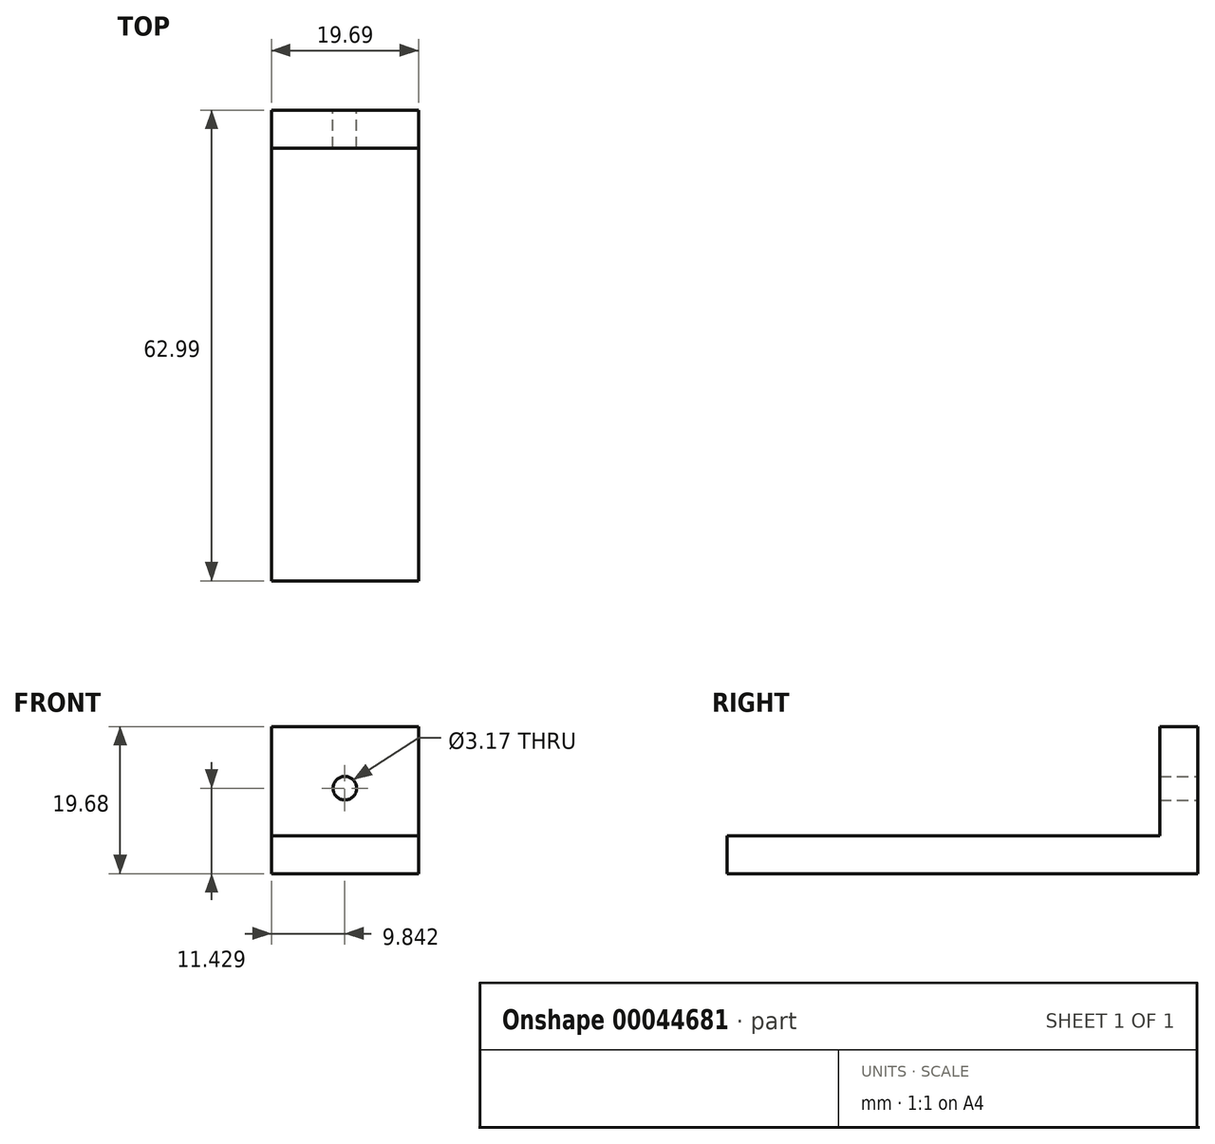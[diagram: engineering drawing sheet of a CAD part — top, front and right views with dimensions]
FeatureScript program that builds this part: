
annotation { "Feature Type Name" : "Feature", "Feature Type Description" : "" }
export const myFeature = defineFeature(function(context is Context, id is Id, definition is map)
    precondition{}
    {
        {
            var Q0;
            Q0=qCreatedBy(makeId("Right.planeOp"),FACE);
            var sketch = newSketch(context, id + "F0", { "sketchPlane" : qUnion([Q0])});
            skLineSegment(sketch, "E0", {"start": v(-35.25, -15.6) * mm, "end": v(27.74, -15.6) * mm});
            skLineSegment(sketch, "E1", {"start": v(27.74, -15.6) * mm, "end": v(27.74, 4.08) * mm});
            skLineSegment(sketch, "E2", {"start": v(27.74, 4.08) * mm, "end": v(22.66, 4.08) * mm});
            skLineSegment(sketch, "E3", {"start": v(22.66, 4.08) * mm, "end": v(22.66, -10.52) * mm});
            skLineSegment(sketch, "E4", {"start": v(22.66, -10.52) * mm, "end": v(-35.25, -10.52) * mm});
            skLineSegment(sketch, "E5", {"start": v(-35.25, -10.52) * mm, "end": v(-35.25, -15.6) * mm});
            skSolve(sketch);
        }
        {
            var Q0;
            Q0=makeQuery(id+"F0.imprint","IMPRINT",FACE,{"disambiguationData":[TD([[makeQuery(id+"F0.imprint","IMPRINT",EDGE,{"derivedFrom":sQuery(id+"F0.wireOp",EDGE,"E0")}),1.0]])]});
            extrude(context, id + "F1", {"entities" : qUnion([Q0]), "depth" : 19.68 * mm});
        }
        {
            var Q0;
            Q0=makeQuery(id+"F1.opExtrude","SWEPT_FACE",FACE,{"disambiguationData":[OSD([sQuery(id+"F0.wireOp",EDGE,"E1")])]});
            var sketch = newSketch(context, id + "F2", { "sketchPlane" : qUnion([Q0])});
            skPoint(sketch, "E6", {"position": v(-9.84, -4.17) * mm});
            skSolve(sketch);
        }
        {
            var Q0;
            Q0=sQuery(id+"F2.wireOp",VERTEX,"E6");
            var Q1;
            Q1=makeQuery(id+"F1.opExtrude","SWEPT_BODY",BODY,{"disambiguationData":[OSD([sQuery(id+"F0.wireOp",EDGE,"E0"),sQuery(id+"F0.wireOp",EDGE,"E1"),sQuery(id+"F0.wireOp",EDGE,"E2"),sQuery(id+"F0.wireOp",EDGE,"E3"),sQuery(id+"F0.wireOp",EDGE,"E4"),sQuery(id+"F0.wireOp",EDGE,"E5")])]});
            hole(context, id + "F3", {"style" : HoleStyle.SIMPLE, "holeDiameter" : 3.17 * mm, "endStyle" : HoleEndStyle.THROUGH, "locations" : qUnion([Q0]), "scope" : qUnion([Q1])});
        }
    });
